# Revit family: 25-HLI
name_source: partatom
category: Plumbing Fixtures
revit_build: Autodesk Revit 2014 (Build: 20130308_1515(x64)
units: mm (PartAtom-declared; Revit-internal decimal feet)

## types (1)
- 25-HLI
    Body = Iron, Cast
    CW Connection = Yes
    Description = Floor Drain, Three Outlets, Round Head With Seat Ceramic Insert
    Documentation = http://www.helvex.com.mx
    Dome = Forged Brass
    Drain = Stainless Steel
    Elevation Range = 0.16" - 1.4"
    Features = Cesspool Integrated; Double Drain Plate; Perimeter Eviction Slot 6 mm; 10 mm Maximum Thickness to Insert
    Installation Thread Lower = 1 ½" - 11 NPSM
    Installation Thread Upper = 2" - 11 ½" NPSM
    Manufacturer = Helvex
    Maximum Height = 7"
    Minimum Height = 6"
    Model = 25-HLI
    Plate Diameter = 7"
    Type Comments = Drains
    URL = http://www.helvex.com.mx
    Vent Connection = Yes

## geometry (parser evidence)
native form markers: Sweep x1
no freeform markers — native parametric forms only
